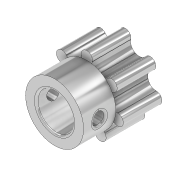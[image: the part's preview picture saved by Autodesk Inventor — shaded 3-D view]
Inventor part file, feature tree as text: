
AUTODESK INVENTOR PART (.ipt)
format: ipt  version: 2020 (Build 240168000, 168)  size: 309,248 bytes
history: native  units: in
note: dims shown in document units (in); Inventor stores cm internally (conversion verified against a paired STEP export)
features: extrude x3, sketch x3, chamfer x1, fillet x1
ambient origin geometry x8: Origin, YZ Plane, XZ Plane, XY Plane, X Axis, Y Axis, Z Axis, Center Point
bodies: Solid1 (feature_tree)
feature tree (8):
  extrude  "Extrusion1"  Depth=0.4724in
  extrude  "Extrusion2"  Depth=0.084in
  extrude  "Extrusion3"  Depth=0.084in
  chamfer  "Chamfer1"  Distance=2.7559in Angle=360.0deg
  fillet  "Fillet1"  Radius=0.2362in
  sketch  "Sketch1"  dims[d0=0.2047in d1=0.4724in]
  sketch  "Sketch2"  dims[d2=0.0866in d5=0.084in]
  sketch  "Sketch3"  dims[d6=0.084in d7=0.084in d8=2.7559in d10=360.0deg d12=0.2362in d13=0.0in d14=0.1969in d15=0.0in d16=0.0748in d17=0.1575in d18=0.0in d19=0.2756in d20=0.125in d21=0.0137in d22=0.0118in d23=0.0079in d24=0.3543in d25=0.0344in d26=0.5in d27=0.0344in]
